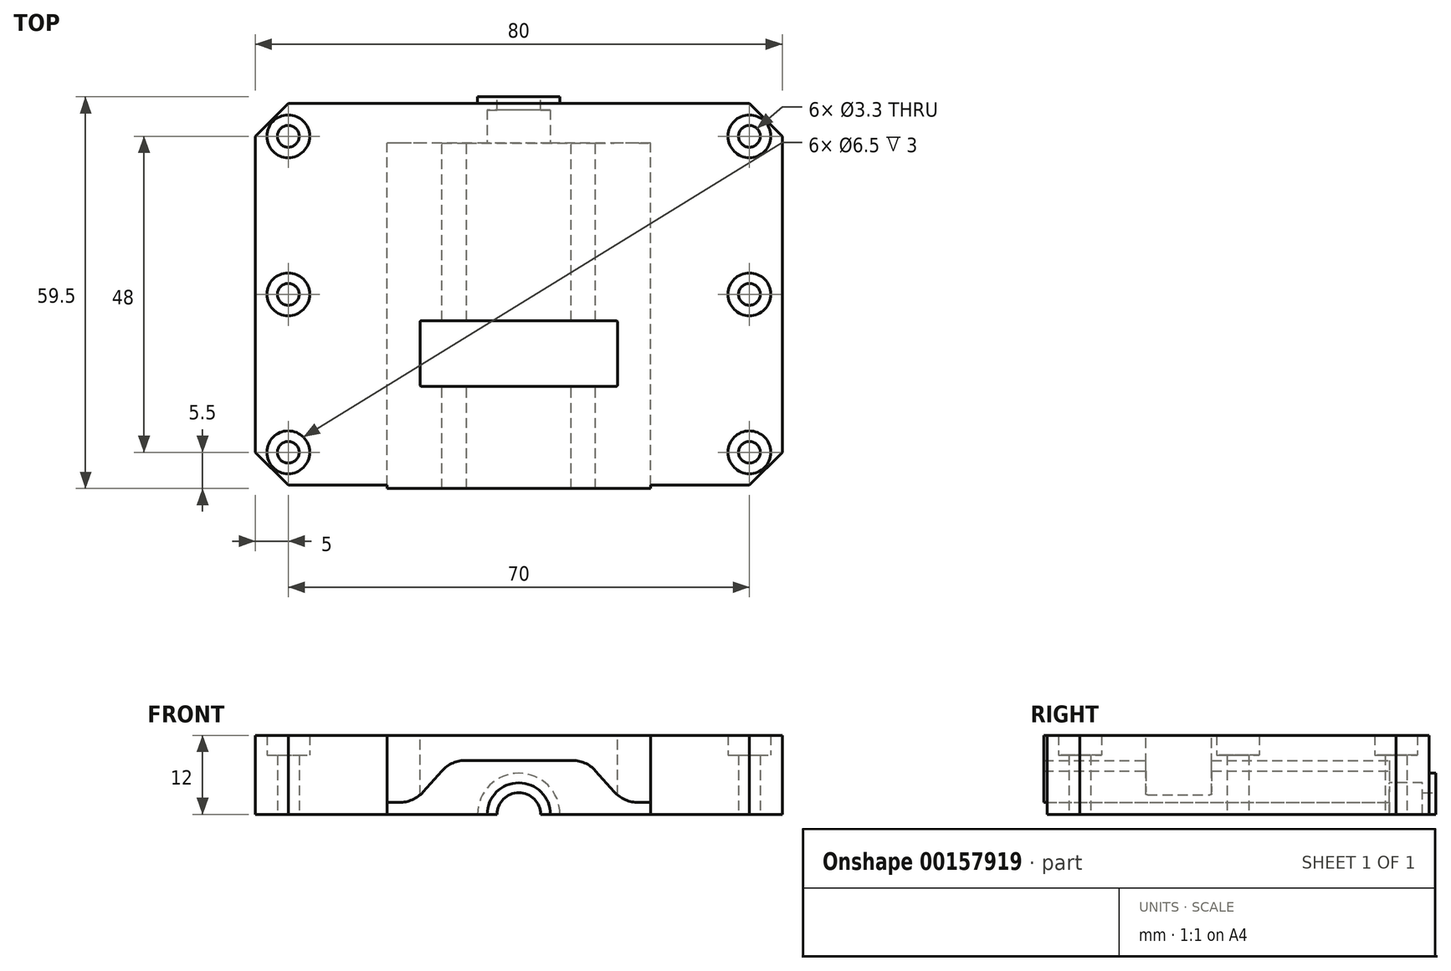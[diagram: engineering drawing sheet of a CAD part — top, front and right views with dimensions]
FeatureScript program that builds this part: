
annotation { "Feature Type Name" : "Feature", "Feature Type Description" : "" }
export const myFeature = defineFeature(function(context is Context, id is Id, definition is map)
    precondition{}
    {
        {
            var Q0;
            Q0=qCreatedBy(makeId("Top.planeOp"),FACE);
            var sketch = newSketch(context, id + "F0", { "sketchPlane" : qUnion([Q0])});
            skLineSegment(sketch, "E0.left", {"start": v(-40, 29) * mm, "end": v(-40, -29) * mm});
            skLineSegment(sketch, "E0.right", {"start": v(40, 29) * mm, "end": v(40, -29) * mm});
            skLineSegment(sketch, "E1", {"start": v(40, 29) * mm, "end": v(-40, 29) * mm});
            skLineSegment(sketch, "E2", {"start": v(40, -29) * mm, "end": v(-40, -29) * mm});
            skSolve(sketch);
        }
        {
            var Q0;
            Q0 = qSketchRegion(id + "F0", true);
            extrude(context, id + "F1", {"entities" : qUnion([Q0]), "oppositeDirection" : true, "depth" : 12 * mm, "symmetric" : true});
        }
        {
            var Q0;
            Q0=qCreatedBy(makeId("Front.planeOp"),FACE);
            var sketch = newSketch(context, id + "F2", { "sketchPlane" : qUnion([Q0])});
            skArc(sketch, "E3.0", {"start": v(-18.2, -4.2) * mm, "mid": v(-16.18, -3.78) * mm, "end": v(-14.5, -2.57) * mm});
            skArc(sketch, "E4.0", {"start": v(-7.93, 2.2) * mm, "mid": v(-9.99, 1.83) * mm, "end": v(-11.66, 0.56) * mm});
            skLineSegment(sketch, "E5", {"start": v(-7.93, 2.2) * mm, "end": v(7.93, 2.2) * mm});
            skLineSegment(sketch, "E6", {"start": v(-18.2, -4.2) * mm, "end": v(-20, -4.2) * mm});
            skLineSegment(sketch, "E7", {"start": v(-11.66, 0.56) * mm, "end": v(-14.5, -2.57) * mm});
            skLineSegment(sketch, "E8.0", {"start": v(20, -6) * mm, "end": v(-20, -6) * mm});
            skPoint(sketch, "E9.orphan", {"position": v(-40, -6) * mm});
            skLineSegment(sketch, "E10", {"start": v(-20, -4.2) * mm, "end": v(-20, -6) * mm});
            skArc(sketch, "E11.MirrorCS", {"start": v(7.93, 2.2) * mm, "mid": v(9.99, 1.83) * mm, "end": v(11.66, 0.56) * mm});
            skLineSegment(sketch, "E12.MirrorCS", {"start": v(11.66, 0.56) * mm, "end": v(14.5, -2.57) * mm});
            skArc(sketch, "E13.MirrorCS", {"start": v(18.2, -4.2) * mm, "mid": v(16.18, -3.78) * mm, "end": v(14.5, -2.57) * mm});
            skLineSegment(sketch, "E14.MirrorCS", {"start": v(18.2, -4.2) * mm, "end": v(20, -4.2) * mm});
            skLineSegment(sketch, "E15.MirrorCS", {"start": v(20, -4.2) * mm, "end": v(20, -6) * mm});
            skPoint(sketch, "E16.orphan", {"position": v(40, -6) * mm});
            skSolve(sketch);
        }
        {
            var Q0;
            Q0 = qSketchRegion(id + "F2", true);
            extrude(context, id + "F3", {"entities" : qUnion([Q0]), "operationType" : NewBodyOperationType.REMOVE, "depth" : 120 * mm, "symmetric" : true});
        }
        {
            var Q0;
            Q0=makeQuery(id+"F1.opExtrude","SWEPT_EDGE",EDGE,{"disambiguationData":[OSD([sQuery(id+"F0.wireOp",EDGE,"E0.left"),sQuery(id+"F0.wireOp",EDGE,"E1")])]});
            var Q1;
            Q1=makeQuery(id+"F1.opExtrude","SWEPT_EDGE",EDGE,{"disambiguationData":[OSD([sQuery(id+"F0.wireOp",EDGE,"E0.left"),sQuery(id+"F0.wireOp",EDGE,"E2")])]});
            var Q2;
            Q2=makeQuery(id+"F1.opExtrude","SWEPT_EDGE",EDGE,{"disambiguationData":[OSD([sQuery(id+"F0.wireOp",EDGE,"E0.right"),sQuery(id+"F0.wireOp",EDGE,"E2")])]});
            var Q3;
            Q3=makeQuery(id+"F1.opExtrude","SWEPT_EDGE",EDGE,{"disambiguationData":[OSD([sQuery(id+"F0.wireOp",EDGE,"E0.right"),sQuery(id+"F0.wireOp",EDGE,"E1")])]});
            chamfer(context, id + "F4", {"entities" : qUnion([Q0, Q1, Q2, Q3]), "width" : 5 * mm, "tangentPropagation" : true});
        }
        {
            var Q0;
            Q0=makeQuery(id+"F1.opExtrude","CAP_FACE",FACE,{"disambiguationData":[OSD([sQuery(id+"F0.wireOp",EDGE,"E0.left"),sQuery(id+"F0.wireOp",EDGE,"E0.right"),sQuery(id+"F0.wireOp",EDGE,"E1"),sQuery(id+"F0.wireOp",EDGE,"E2")])],"isStart":true});
            var sketch = newSketch(context, id + "F5", { "sketchPlane" : qUnion([Q0])});
            skPoint(sketch, "E17", {"position": v(35, 24) * mm});
            skPoint(sketch, "E18.MirrorP", {"position": v(-35, 24) * mm});
            skPoint(sketch, "E19.MirrorP", {"position": v(-35, -24) * mm});
            skPoint(sketch, "E20.MirrorP", {"position": v(35, -24) * mm});
            skPoint(sketch, "E21", {"position": v(-35, 0) * mm});
            skPoint(sketch, "E22", {"position": v(35, 0) * mm});
            skSolve(sketch);
        }
        {
            var Q0;
            Q0=sQuery(id+"F5.wireOp",VERTEX,"E18.MirrorP");
            var Q1;
            Q1=sQuery(id+"F5.wireOp",VERTEX,"E17");
            var Q2;
            Q2=sQuery(id+"F5.wireOp",VERTEX,"E22");
            var Q3;
            Q3=sQuery(id+"F5.wireOp",VERTEX,"E20.MirrorP");
            var Q4;
            Q4=sQuery(id+"F5.wireOp",VERTEX,"E19.MirrorP");
            var Q5;
            Q5=sQuery(id+"F5.wireOp",VERTEX,"E21");
            var Q6;
            Q6=makeQuery(id+"F1.opExtrude","SWEPT_BODY",BODY,{"disambiguationData":[OSD([sQuery(id+"F0.wireOp",EDGE,"E0.left"),sQuery(id+"F0.wireOp",EDGE,"E0.right"),sQuery(id+"F0.wireOp",EDGE,"E1"),sQuery(id+"F0.wireOp",EDGE,"E2")])]});
            hole(context, id + "F6", {"style" : HoleStyle.C_BORE, "endStyle" : HoleEndStyle.THROUGH, "standardTappedOrClearance" : lookupTablePath({ "standard" : "ISO", "fit" : "Normal", "size" : "M3", "type" : "Clearance" }), "standardBlindInLast" : lookupTablePath({ "fit" : "Standard", "standard" : "ISO", "size" : "M3", "type" : "Clearance" }), "holeDiameter" : 3.3 * mm, "cBoreDiameter" : 6.5 * mm, "cBoreDepth" : 3 * mm, "locations" : qUnion([Q0, Q1, Q2, Q3, Q4, Q5]), "scope" : qUnion([Q6]), "isTappedThrough" : true, "startStyle" : HoleStartStyle.SKETCH});
        }
        {
            var Q0;
            Q0=makeQuery(id+"F1.opExtrude","SWEPT_FACE",FACE,{"disambiguationData":[OSD([sQuery(id+"F0.wireOp",EDGE,"E2")])]});
            var sketch = newSketch(context, id + "F7", { "sketchPlane" : qUnion([Q0])});
            skLineSegment(sketch, "E23", {"start": v(-20, -4.2) * mm, "end": v(-20, 6) * mm});
            skLineSegment(sketch, "E24", {"start": v(-20, 6) * mm, "end": v(20, 6) * mm});
            skLineSegment(sketch, "E25", {"start": v(20, 6) * mm, "end": v(20, -4.2) * mm});
            skArc(sketch, "E26.0", {"start": v(18.2, -4.2) * mm, "mid": v(16.18, -3.78) * mm, "end": v(14.5, -2.57) * mm});
            skLineSegment(sketch, "E27.0", {"start": v(18.2, -4.2) * mm, "end": v(20, -4.2) * mm});
            skLineSegment(sketch, "E28.0", {"start": v(11.66, 0.56) * mm, "end": v(14.5, -2.57) * mm});
            skArc(sketch, "E29.0", {"start": v(7.93, 2.2) * mm, "mid": v(9.99, 1.83) * mm, "end": v(11.66, 0.56) * mm});
            skLineSegment(sketch, "E30.0", {"start": v(-7.93, 2.2) * mm, "end": v(7.93, 2.2) * mm});
            skArc(sketch, "E31.0", {"start": v(-7.93, 2.2) * mm, "mid": v(-9.99, 1.83) * mm, "end": v(-11.66, 0.56) * mm});
            skLineSegment(sketch, "E32.0", {"start": v(-11.66, 0.56) * mm, "end": v(-14.5, -2.57) * mm});
            skArc(sketch, "E33.0", {"start": v(-18.2, -4.2) * mm, "mid": v(-16.18, -3.78) * mm, "end": v(-14.5, -2.57) * mm});
            skSolve(sketch);
        }
        {
            var Q0;
            Q0=makeQuery(id+"F7.imprint","IMPRINT",FACE,{"disambiguationData":[TD([[makeQuery(id+"F7.imprint","IMPRINT",EDGE,{"derivedFrom":sQuery(id+"F7.wireOp",EDGE,"E23")}),-1.0]])]});
            extrude(context, id + "F8", {"entities" : qUnion([Q0]), "operationType" : NewBodyOperationType.ADD, "depth" : 0.5 * mm});
        }
        {
            var Q0;
            Q0=makeQuery(id+"F1.opExtrude","SWEPT_FACE",FACE,{"disambiguationData":[OSD([sQuery(id+"F0.wireOp",EDGE,"E1")])]});
            var sketch = newSketch(context, id + "F9", { "sketchPlane" : qUnion([Q0])});
            skLineSegment(sketch, "E34", {"start": v(-20, -6) * mm, "end": v(-3.3, -6) * mm});
            skLineSegment(sketch, "E35.0", {"start": v(7.93, 2.2) * mm, "end": v(-7.93, 2.2) * mm});
            skArc(sketch, "E36.0", {"start": v(7.93, 2.2) * mm, "mid": v(9.99, 1.83) * mm, "end": v(11.66, 0.56) * mm});
            skLineSegment(sketch, "E37.0", {"start": v(11.66, 0.56) * mm, "end": v(14.5, -2.57) * mm});
            skArc(sketch, "E38.0", {"start": v(18.2, -4.2) * mm, "mid": v(16.18, -3.78) * mm, "end": v(14.5, -2.57) * mm});
            skLineSegment(sketch, "E39.0", {"start": v(18.2, -4.2) * mm, "end": v(20, -4.2) * mm});
            skLineSegment(sketch, "E40.0", {"start": v(20, -4.2) * mm, "end": v(20, -6) * mm});
            skArc(sketch, "E41.0", {"start": v(-7.93, 2.2) * mm, "mid": v(-9.99, 1.83) * mm, "end": v(-11.66, 0.56) * mm});
            skLineSegment(sketch, "E42.0", {"start": v(-11.66, 0.56) * mm, "end": v(-14.5, -2.57) * mm});
            skArc(sketch, "E43.0", {"start": v(-18.2, -4.2) * mm, "mid": v(-16.18, -3.78) * mm, "end": v(-14.5, -2.57) * mm});
            skLineSegment(sketch, "E44.0", {"start": v(-18.2, -4.2) * mm, "end": v(-20, -4.2) * mm});
            skLineSegment(sketch, "E45.0", {"start": v(-20, -4.2) * mm, "end": v(-20, -6) * mm});
            skArc(sketch, "E46", {"start": v(3.3, -6) * mm, "mid": v(0, -2.7) * mm, "end": v(-3.3, -6) * mm});
            skLineSegment(sketch, "E47.trimOffspring", {"start": v(3.3, -6) * mm, "end": v(20, -6) * mm});
            skSolve(sketch);
        }
        {
            var Q0;
            Q0 = qSketchRegion(id + "F9", true);
            extrude(context, id + "F10", {"entities" : qUnion([Q0]), "operationType" : NewBodyOperationType.ADD, "oppositeDirection" : true, "depth" : 6 * mm});
        }
        {
            var Q0;
            Q0=makeQuery(id+"F10.opExtrude","CAP_FACE",FACE,{"disambiguationData":[OSD([sQuery(id+"F9.wireOp",EDGE,"E34"),sQuery(id+"F9.wireOp",EDGE,"E35.0"),sQuery(id+"F9.wireOp",EDGE,"E36.0"),sQuery(id+"F9.wireOp",EDGE,"E37.0"),sQuery(id+"F9.wireOp",EDGE,"E38.0"),sQuery(id+"F9.wireOp",EDGE,"E39.0"),sQuery(id+"F9.wireOp",EDGE,"E40.0"),sQuery(id+"F9.wireOp",EDGE,"E41.0"),sQuery(id+"F9.wireOp",EDGE,"E42.0"),sQuery(id+"F9.wireOp",EDGE,"E43.0"),sQuery(id+"F9.wireOp",EDGE,"E44.0"),sQuery(id+"F9.wireOp",EDGE,"E45.0"),sQuery(id+"F9.wireOp",EDGE,"E46"),sQuery(id+"F9.wireOp",EDGE,"E47.trimOffspring")])],"isStart":false});
            var sketch = newSketch(context, id + "F11", { "sketchPlane" : qUnion([Q0])});
            skArc(sketch, "E48.0", {"start": v(-3.3, -6) * mm, "mid": v(0, -2.7) * mm, "end": v(3.3, -6) * mm});
            skCircle(sketch, "E49", {"center": v(0, -6) * mm, "radius": 4.8 * mm});
            skSolve(sketch);
        }
        {
            var Q0;
            Q0 = qSketchRegion(id + "F11", true);
            extrude(context, id + "F12", {"entities" : qUnion([Q0]), "operationType" : NewBodyOperationType.REMOVE, "oppositeDirection" : true, "depth" : 5 * mm});
        }
        {
            var Q0;
            Q0=makeQuery(id+"F10.boolean.opBoolean","MERGE",FACE,{"derivedFrom":[makeQuery(id+"F1.opExtrude","SWEPT_FACE",FACE,{"disambiguationData":[OSD([sQuery(id+"F0.wireOp",EDGE,"E1")])]}),makeQuery(id+"F10.opExtrude","CAP_FACE",FACE,{"disambiguationData":[OSD([sQuery(id+"F9.wireOp",EDGE,"E34"),sQuery(id+"F9.wireOp",EDGE,"E35.0"),sQuery(id+"F9.wireOp",EDGE,"E36.0"),sQuery(id+"F9.wireOp",EDGE,"E37.0"),sQuery(id+"F9.wireOp",EDGE,"E38.0"),sQuery(id+"F9.wireOp",EDGE,"E39.0"),sQuery(id+"F9.wireOp",EDGE,"E40.0"),sQuery(id+"F9.wireOp",EDGE,"E41.0"),sQuery(id+"F9.wireOp",EDGE,"E42.0"),sQuery(id+"F9.wireOp",EDGE,"E43.0"),sQuery(id+"F9.wireOp",EDGE,"E44.0"),sQuery(id+"F9.wireOp",EDGE,"E45.0"),sQuery(id+"F9.wireOp",EDGE,"E46"),sQuery(id+"F9.wireOp",EDGE,"E47.trimOffspring")])],"isStart":true})]});
            var sketch = newSketch(context, id + "F13", { "sketchPlane" : qUnion([Q0])});
            skArc(sketch, "E50.0", {"start": v(3.3, -6) * mm, "mid": v(0, -2.7) * mm, "end": v(-3.3, -6) * mm});
            skArc(sketch, "E51", {"start": v(6.25, -6) * mm, "mid": v(0, 0.25) * mm, "end": v(-6.25, -6) * mm});
            skLineSegment(sketch, "E52", {"start": v(3.3, -6) * mm, "end": v(6.25, -6) * mm});
            skLineSegment(sketch, "E53", {"start": v(-6.25, -6) * mm, "end": v(-3.3, -6) * mm});
            skSolve(sketch);
        }
        {
            var Q0;
            Q0 = qSketchRegion(id + "F13", true);
            extrude(context, id + "F14", {"entities" : qUnion([Q0]), "operationType" : NewBodyOperationType.ADD, "depth" : 1 * mm});
        }
        {
            var Q0;
            Q0=makeQuery(id+"F8.boolean.opBoolean","MERGE",FACE,{"derivedFrom":[makeQuery(id+"F1.opExtrude","CAP_FACE",FACE,{"disambiguationData":[OSD([sQuery(id+"F0.wireOp",EDGE,"E0.left"),sQuery(id+"F0.wireOp",EDGE,"E0.right"),sQuery(id+"F0.wireOp",EDGE,"E1"),sQuery(id+"F0.wireOp",EDGE,"E2")])],"isStart":true}),makeQuery(id+"F8.opExtrude","SWEPT_FACE",FACE,{"disambiguationData":[OSD([sQuery(id+"F7.wireOp",EDGE,"E24")])]})]});
            var sketch = newSketch(context, id + "F15", { "sketchPlane" : qUnion([Q0])});
            skLineSegment(sketch, "E54.bottom", {"start": v(-14.75, -4) * mm, "end": v(14.75, -4) * mm});
            skLineSegment(sketch, "E54.top", {"start": v(-14.75, -14) * mm, "end": v(14.75, -14) * mm});
            skLineSegment(sketch, "E54.left", {"start": v(-15, -4.25) * mm, "end": v(-15, -13.75) * mm});
            skLineSegment(sketch, "E54.right", {"start": v(15, -4.25) * mm, "end": v(15, -13.75) * mm});
            skPoint(sketch, "E55.visualSharp", {"position": v(-15, -4) * mm});
            skArc(sketch, "E55.filletArc", {"start": v(-14.75, -4) * mm, "mid": v(-14.93, -4.07) * mm, "end": v(-15, -4.25) * mm});
            skPoint(sketch, "E56.visualSharp", {"position": v(-15, -14) * mm});
            skArc(sketch, "E56.filletArc", {"start": v(-15, -13.75) * mm, "mid": v(-14.93, -13.93) * mm, "end": v(-14.75, -14) * mm});
            skPoint(sketch, "E57.visualSharp", {"position": v(15, -14) * mm});
            skArc(sketch, "E57.filletArc", {"start": v(14.75, -14) * mm, "mid": v(14.93, -13.93) * mm, "end": v(15, -13.75) * mm});
            skPoint(sketch, "E58.visualSharp", {"position": v(15, -4) * mm});
            skArc(sketch, "E58.filletArc", {"start": v(15, -4.25) * mm, "mid": v(14.93, -4.07) * mm, "end": v(14.75, -4) * mm});
            skSolve(sketch);
        }
        {
            var Q0;
            Q0 = qSketchRegion(id + "F15", true);
            extrude(context, id + "F16", {"entities" : qUnion([Q0]), "operationType" : NewBodyOperationType.REMOVE, "endBound" : BoundingType.THROUGH_ALL, "oppositeDirection" : true, "depth" : 25 * mm});
        }
    });
